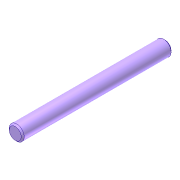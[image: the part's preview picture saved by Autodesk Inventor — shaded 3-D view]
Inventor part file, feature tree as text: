
AUTODESK INVENTOR PART (.ipt)
format: ipt  version: 2016 (Build 200138000, 138)  size: 80,384 bytes
history: native  units: in
note: dims shown in document units (in); Inventor stores cm internally (conversion verified against a paired STEP export)
features: extrude x1, chamfer x1, sketch x1
ambient origin geometry x8: Origin, YZ Plane, XZ Plane, XY Plane, X Axis, Y Axis, Z Axis, Center Point
bodies: Solid1 (feature_tree)
feature tree (3):
  extrude  "Extrusion42"  Depth=0.3937in
  chamfer  "Chamfer6"  Distance=0.3937in
  sketch  "Sketch47"  dims[d21=0.7874in d264=0.0394in d265=0.3937in d266=0.0in d267=0.0039in d268=0.0787in d269=45.0deg]
